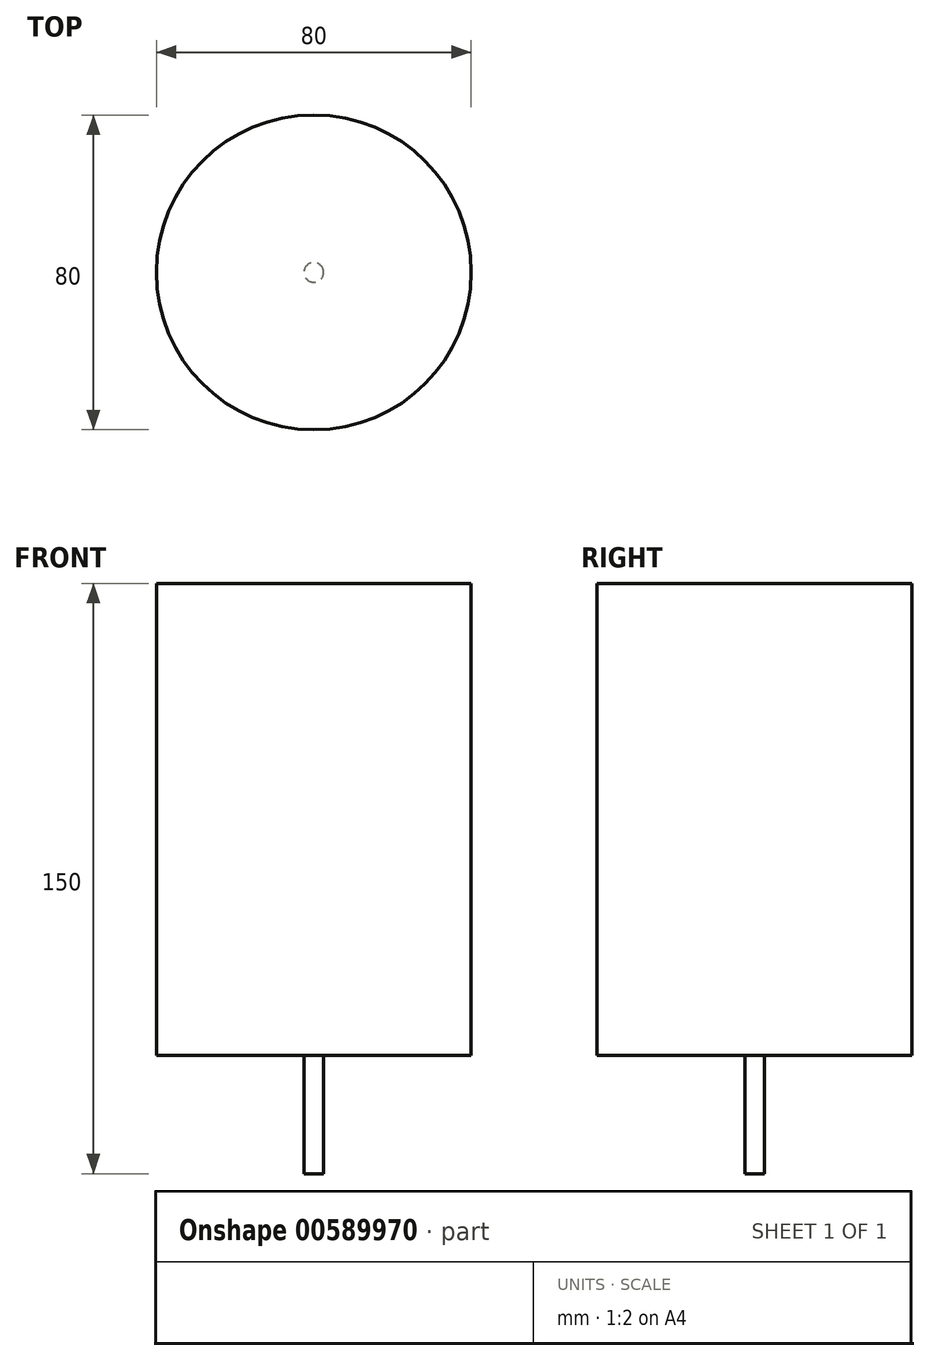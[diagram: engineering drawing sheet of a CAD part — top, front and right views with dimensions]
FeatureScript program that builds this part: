
annotation { "Feature Type Name" : "Feature", "Feature Type Description" : "" }
export const myFeature = defineFeature(function(context is Context, id is Id, definition is map)
    precondition{}
    {
        {
            var Q0;
            Q0=qCreatedBy(makeId("Top.planeOp"),FACE);
            var sketch = newSketch(context, id + "F0", { "sketchPlane" : qUnion([Q0])});
            skCircle(sketch, "E0", {"center": v(0, 0) * mm, "radius": 40 * mm});
            skSolve(sketch);
        }
        {
            var Q0;
            Q0=makeQuery(id+"F0.imprint","IMPRINT",FACE,{"disambiguationData":[TD([[makeQuery(id+"F0.imprint","IMPRINT",EDGE,{"derivedFrom":sQuery(id+"F0.wireOp",EDGE,"E0")}),1.0]])]});
            extrude(context, id + "F1", {"entities" : qUnion([Q0]), "depth" : 120 * mm, "offsetDistance" : 25 * mm});
        }
        {
            var Q0;
            Q0=makeQuery(id+"F1.opExtrude","CAP_FACE",FACE,{"disambiguationData":[OSD([sQuery(id+"F0.wireOp",EDGE,"E0")])],"isStart":true});
            var sketch = newSketch(context, id + "F2", { "sketchPlane" : qUnion([Q0])});
            skCircle(sketch, "E1", {"center": v(0, 0) * mm, "radius": 2.5 * mm});
            skSolve(sketch);
        }
        {
            var Q0;
            Q0 = qSketchRegion(id + "F2", true);
            extrude(context, id + "F3", {"entities" : qUnion([Q0]), "operationType" : NewBodyOperationType.ADD, "depth" : 25 * mm, "offsetDistance" : 25 * mm});
        }
        {
            var Q0;
            Q0=makeQuery(id+"F2.imprint","IMPRINT",FACE,{"disambiguationData":[TD([[makeQuery(id+"F2.imprint","IMPRINT",EDGE,{"derivedFrom":sQuery(id+"F2.wireOp",EDGE,"E1")}),1.0]])]});
            extrude(context, id + "F4", {"entities" : qUnion([Q0]), "operationType" : NewBodyOperationType.ADD, "depth" : 30 * mm, "offsetDistance" : 25 * mm});
        }
    });
